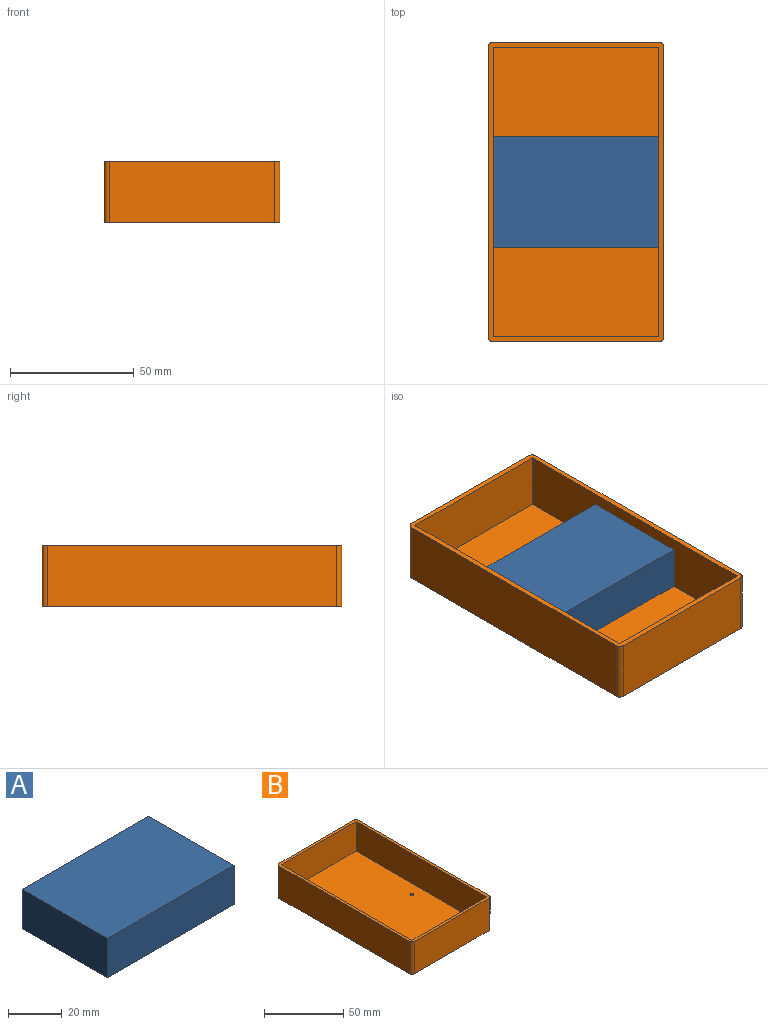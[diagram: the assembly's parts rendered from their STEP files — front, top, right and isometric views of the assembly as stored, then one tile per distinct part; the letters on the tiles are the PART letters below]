
ASSEMBLY  parts=2 mates=1
PART A: 6 faces, bbox 67x45x18 mm
  f0: plane 67x18mm, normal (0,-1,0), area 1206mm2, adj f1,f3,f4,f5
  f1: plane 45x18mm, normal (1,0,0), area 810mm2, adj f0,f2,f4,f5
  f2: plane 67x18mm, normal (0,1,0), area 1206mm2, adj f1,f3,f4,f5
  f3: plane 45x18mm, normal (-1,0,0), area 810mm2, adj f0,f2,f4,f5
  f4: plane 67x45mm, normal (0,0,1), area 3015mm2, adj f0,f1,f2,f3
  f5: plane 67x45mm, normal (0,0,-1), area 3015mm2, adj f0,f1,f2,f3
PART B: 17 faces, bbox 71x121x25 mm
  f0: plane 121x71mm, normal (0,0,1), area 748.6mm2, adj f1,f2,f3,f4,f6,f7,f8,f9
  f1: plane 67x25mm, normal (0,-1,0), area 1675mm2, adj f0,f5,f13,f14
  f2: plane 117x25mm, normal (1,0,0), area 2925mm2, adj f0,f5,f14,f15
  f3: plane 67x25mm, normal (0,1,0), area 1675mm2, adj f0,f5,f15,f16
  f4: plane 117x25mm, normal (-1,0,0), area 2925mm2, adj f0,f5,f13,f16
  f5: plane 121x71mm, normal (0,0,-1), area 8577.7mm2, adj f1,f2,f3,f4,f11,f12,f13,f14
  f6: plane 67x23mm, normal (0,1,0), area 1541mm2, adj f0,f7,f9,f10
  f7: plane 117x23mm, normal (-1,0,0), area 2691mm2, adj f0,f6,f8,f10
  f8: plane 67x23mm, normal (0,-1,0), area 1541mm2, adj f0,f7,f9,f10
  f9: plane 117x23mm, normal (1,0,0), area 2691mm2, adj f0,f6,f8,f10
  f10: plane 117x67mm, normal (0,0,1), area 7829.2mm2, adj f6,f7,f8,f9,f11,f12
  f11: cylinder r=1.25mm len=2.5mm, axis (0,0,1), area 15.7mm2, adj f5,f10
  f12: cylinder r=1.25mm len=2.5mm, axis (0,0,1), area 15.7mm2, adj f5,f10
  f13: cylinder r=2mm len=25mm, axis (0,0,1), area 78.5mm2, adj f0,f1,f4,f5
  f14: cylinder r=2mm len=25mm, axis (0,0,-1), area 78.5mm2, adj f0,f1,f2,f5
  f15: cylinder r=2mm len=25mm, axis (0,0,1), area 78.5mm2, adj f0,f2,f3,f5
  f16: cylinder r=2mm len=25mm, axis (0,0,-1), area 78.5mm2, adj f0,f3,f4,f5
PLACE A t=(8.15,5.4,-6.96)mm
PLACE B t=(8.15,5.4,-8.96)mm
MATE fastened A.f5 <-> B.f10  axis (0,0,-1) through (8.15,5.4,-6.96)mm
